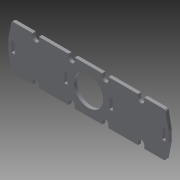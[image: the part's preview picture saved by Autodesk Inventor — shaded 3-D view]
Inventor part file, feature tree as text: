
AUTODESK INVENTOR PART (.ipt)
format: ipt  version: 2013 (Build 170138000, 138)  size: 191,488 bytes
history: native  units: mm
features: extrude x1, sketch x1
ambient origin geometry x8: Origin, YZ Plane, XZ Plane, XY Plane, X Axis, Y Axis, Z Axis, Center Point
bodies: Solid1 (feature_tree)
feature tree (2):
  extrude  "Extrusion1"  Depth=28.0mm
  sketch  "Sketch1"  dims[d2=42.0mm d3=28.0mm d4=76.0mm d5=21.0mm d6=3.0mm d7=10.0mm d8=20.0mm d9=3.0mm d10=10.0mm d11=20.0mm d12=3.0mm d13=10.0mm d14=3.0mm d15=3.0mm d16=10.0mm d17=3.0mm d18=5.0mm d19=5.0mm d20=6.0mm d21=16.0mm d22=3.0mm d23=3.0mm d24=6.0mm d25=16.0mm d26=6.0mm d27=16.0mm d28=6.0mm d29=16.0mm d30=3.0mm d31=3.0mm d32=6.0mm d33=50.0mm d34=3.0mm d35=50.0mm d36=3.0mm d37=0.0mm d38=76.0mm d39=21.0mm d40=3.0mm d41=3.0mm d42=10.0mm d43=10.0mm d44=21.0mm d45=2.0mm d46=50.0mm d47=50.0mm d48=3.0mm d49=3.0mm d50=3.0mm d51=3.0mm d52=3.0mm d53=3.0mm d54=3.0mm d55=3.0mm d56=17.561443mm]
